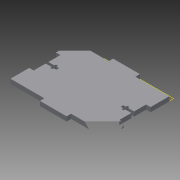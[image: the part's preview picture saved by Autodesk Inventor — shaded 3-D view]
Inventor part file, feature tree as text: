
AUTODESK INVENTOR PART (.ipt)
format: ipt  version: 2014 (Build 180170000, 170)  size: 150,528 bytes
history: native  units: mm
features: reference x5, extrude x4, sketch x4, plane x3, other x3
ambient origin geometry x8: Origin, YZ Plane, XZ Plane, XY Plane, X Axis, Y Axis, Z Axis, Center Point
bodies: Body1 (feature_tree)
feature tree (19):
  plane  "工作平面1"
  extrude  "拉伸2"  Depth=5.0mm TaperAngle=0.0deg
  sketch  "草图3"  dims[d6=10.0mm d7=0.0mm]
  plane  "工作平面2"
  extrude  "拉伸3"  Depth=2.4mm TaperAngle=0.0deg
  sketch  "草图4"  dims[d8=3.0mm d9=12.0mm d10=6.5mm d11=2.4mm d12=8.0mm d13=10.0mm d14=0.0mm]
  plane  "工作平面3"
  extrude  "拉伸4"  [1 undecoded]
  extrude  "拉伸5"  [1 undecoded]
  sketch  "草图2"  dims[d2=5.0mm d3=0.0mm d4=10.0mm d5=0.0mm]
  reference  "参考5"
  reference  "参考6"
  reference  "参考7"
  sketch  "草图5"
  reference  "参考8"
  reference  "参考9"
  other  "slot"
  other  "slot:1"
  other  "slot:2"
note: 2 required parameter values undecoded (feature->parameter linkage not recoverable at this tier; creation-order binding heuristic only, values carry confidence <= 0.55)
